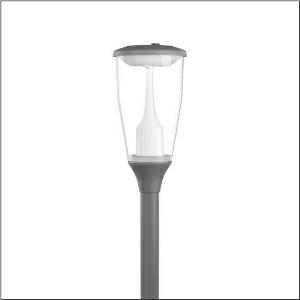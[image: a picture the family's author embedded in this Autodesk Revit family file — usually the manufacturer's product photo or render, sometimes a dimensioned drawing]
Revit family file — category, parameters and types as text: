
# Revit family: dl_11_iq___st1_2a_5xa5575ev14h000022_9f00
name_source: partatom
category: Lighting Fixtures
units: mm (PartAtom-declared; Revit-internal decimal feet)

## family parameters
Cut with Voids When Loaded = No
Host = Face
Light Source = No
Part Type = Normal
Room Calculation Point = No
Round Connector Dimension = Use Diameter
Shared = No

## types (1)
- --- (1 x LED, 1560 lm, 10.7 W, 3000K)
    Apparent Load = 11 VA
    CIE Flux Codes = 24 63 94 96 100
    Color Rendering = 70
    Color Temperature = 3000K
    Default Elevation = 1800 mm
    Description = DL 11 iQ, mast luminaire, Module 540 iQ-SR, primary light control with 3 zone facetted reflector, of plastic, silver coated, highly specular, structured, primary optical cover: cover, of PMMA, transparent, light distribution: ST1.2a, light emission: direct distribution, primary light characteristic: asymmetric, installation type: post-top, LED, High Power LED, rated luminous flux: 1.560lm, luminous efficacy: 146lm/W, light colour: 730, colour temperature: 3000K, control gear: iQ-Street Remote, D4i with power reduction, control: pre-setting: logarithmic dimming characteristic, Street-Remote, Auto-Match, Temp-Guard, Lumen-Switch, Night-Set, Smart-Wire, Light-Fading, Desk-Remote (wireless, voltage-free reading and setting of iQ features in the workshop via application-optimized NFC function/RFID function), optimised constant luminous flux control (CLO 2.0), mains connection: 220..240V, AC, 50/60Hz, connection cable pre-assembled, cable length: 5,5m, start of lifetime: 11W, end of service life: 11W, reduction: 6W, luminaire housing, upper part, of diecast aluminium, coated, Siteco® metallic grey (DB 702S), spigot size: 76mm (post-top), mounting height: 3..5m, post-top mast mounting element, of diecast aluminium, coated, Siteco® metallic grey (DB 702S), Module 540 iQ-SR, traffic white (RAL 9016), equipment: standard, Smart Interface above, protection rating (complete): IP66, insulation class (complete): insulation class II (safety insulation), certification: CE, ENEC, ENEC+, VDE, impact resistance: IK07, packaging unit: 1 piece

Light Distribution: ST1.2a
    Height = 665 mm
    Lamp = 1 x LED
    Lamp Light Flux = 1560 lm
    Lamp Power = 10.7 W
    Lamp count = 1
    Length = 334 mm
    Luminous efficacy = 146 lm/W
    Manufacturer = Siteco
    ModVariant = No
    Model = 5XA5575EV14H000022
    Number of Poles = 1
    OnlyDefault = Yes
    Power Factor = 1
    Product Name = DL 11 iQ | ST1.2a
    Product group = mast luminaire | pylon top
    ProductGroupID = 6100
    Protection Class = Protection class II
    Protection Degree = IP 66
    RLX_Detail_Level = 1
    RLX_Emergency_Light_Flux = 0 lm
    RLX_Emergency_Type = 0
    RLX_Emergency_Type_DB = No
    RlxData = <blob elided: 140593 chars, md5=89a1eb78>
    Socket = socket
    Standby Power = 0 W
    System Light Flux = 1560 lm
    System Power = 11 W
    Type Comments = factory setting: luminous flux: 100 % | dim-lin: 254 | 419 mA
    Type Image = l_1337541.jpg
    URL = http://relux.com
    VarID = @adj_116353
    Voltage = 0 V
    Weight = 0.00 kg
    Width = 0 mm  [stored 0 ft]

note: [stored X ft] marks values corroborated as IEEE doubles in the binary element streams (Revit-internal decimal feet)

## geometry (parser evidence)
native form markers: Blend x4, Sweep x10
no freeform markers — native parametric forms only
